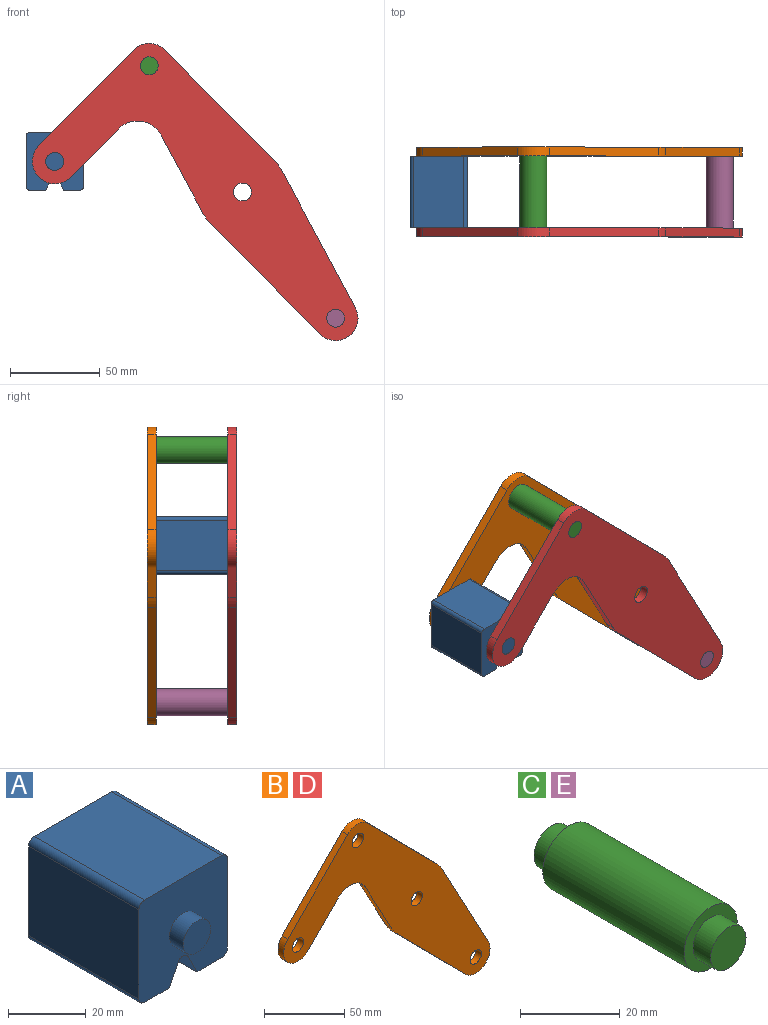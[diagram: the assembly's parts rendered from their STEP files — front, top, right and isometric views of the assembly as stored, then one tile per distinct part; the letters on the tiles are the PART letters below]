
ASSEMBLY  parts=5 mates=3
PART A: 18 faces, bbox 32.1x50x32.1 mm
  f0: plane 40x28.08mm, normal (1,0,0), area 1123.1mm2, adj f4,f10,f13,f14
  f1: plane 40x9.04mm, normal (0,0,-1), area 361.6mm2, adj f2,f4,f10,f14
  f2: plane 40x6.42mm, normal (-0.89,0,-0.45), area 287.2mm2, adj f1,f4,f10,f15
  f3: plane 40x6.42mm, normal (0.89,0,-0.45), area 287.2mm2, adj f4,f5,f10,f15
  f4: plane 32.08x32.08mm, normal (0,-1,0), area 900.6mm2, adj f0,f1,f2,f3,f5,f6,f7,f9
  f5: plane 40x9.04mm, normal (0,0,-1), area 361.6mm2, adj f3,f4,f10,f16
  f6: plane 40x28.08mm, normal (0,0,1), area 1123.1mm2, adj f4,f10,f13,f17
  f7: plane 40x28.08mm, normal (-1,0,0), area 1123.1mm2, adj f4,f10,f16,f17
  f8: plane 10x10mm, normal (0,-1,0), area 78.5mm2, adj f9
  f9: cylinder r=5mm len=10mm, axis (0,1,0), area 157.1mm2, adj f4,f8
  f10: plane 32.08x32.08mm, normal (0,1,0), area 900.6mm2, adj f0,f1,f2,f3,f5,f6,f7,f12
  f11: plane 10x10mm, normal (0,1,0), area 78.5mm2, adj f12
  f12: cylinder r=5mm len=10mm, axis (0,-1,0), area 157.1mm2, adj f10,f11
  f13: cylinder r=2mm len=40mm, axis (0,1,0), area 125.7mm2, adj f0,f4,f6,f10
  f14: cylinder r=2mm len=40mm, axis (0,-1,0), area 125.7mm2, adj f0,f1,f4,f10
  f15: cylinder r=2mm len=40mm, axis (0,1,0), area 177.1mm2, adj f2,f3,f4,f10
  f16: cylinder r=2mm len=40mm, axis (0,1,0), area 125.7mm2, adj f4,f5,f7,f10
  f17: cylinder r=2mm len=40mm, axis (0,-1,0), area 125.7mm2, adj f4,f6,f7,f10
PART B: 18 faces, bbox 181.7x5x165.8 mm
  f0: plane 43.49x23.35mm, normal (-0.88,0,-0.47), area 246.8mm2, adj f1,f14,f16,f17
  f1: cylinder r=25mm len=5.75mm, axis (0,1,0), area 35.8mm2, adj f0,f2,f16,f17
  f2: plane 61.6x60.87mm, normal (-0.71,0,-0.7), area 433mm2, adj f1,f3,f16,f17
  f3: cylinder r=12.5mm len=21.39mm, axis (0,1,0), area 178.4mm2, adj f2,f4,f16,f17
  f4: plane 76.3x40.96mm, normal (0.88,0,0.47), area 433mm2, adj f3,f5,f16,f17
  f5: cylinder r=25mm len=5.75mm, axis (0,1,0), area 35.8mm2, adj f4,f6,f16,f17
  f6: plane 61.6x60.87mm, normal (0.71,0,0.7), area 433mm2, adj f5,f7,f16,f17
  f7: cylinder r=12.5mm len=17.78mm, axis (0,1,0), area 98.9mm2, adj f6,f8,f16,f17
  f8: plane 53.35x52.71mm, normal (-0.71,0,0.7), area 375mm2, adj f7,f9,f16,f17
  f9: cylinder r=12.5mm len=21.39mm, axis (0,1,0), area 196.3mm2, adj f8,f10,f16,f17
  f10: plane 26.86x26.54mm, normal (0.71,0,-0.7), area 188.8mm2, adj f9,f14,f16,f17
  f11: cylinder r=5mm len=10mm, axis (0,1,0), area 157.1mm2, adj f16,f17
  f12: cylinder r=5mm len=10mm, axis (0,1,0), area 157.1mm2, adj f16,f17
  f13: cylinder r=5mm len=10mm, axis (0,1,0), area 157.1mm2, adj f16,f17
  f14: cylinder r=15mm len=23.89mm, axis (0,1,0), area 140.2mm2, adj f0,f10,f16,f17
  f15: cylinder r=5mm len=10mm, axis (0,1,0), area 157.1mm2, adj f16,f17
  f16: plane 181.66x165.78mm, normal (0,-1,0), area 8710.1mm2, adj f0,f1,f2,f3,f4,f5,f6,f7
  f17: plane 181.66x165.78mm, normal (0,1,0), area 8710.1mm2, adj f0,f1,f2,f3,f4,f5,f6,f7
PART C: 7 faces, bbox 15x50x15 mm
  f0: cylinder r=7.5mm len=40mm, axis (0,-1,0), area 1885mm2, adj f2,f5
  f1: cylinder r=5mm len=10mm, axis (0,1,0), area 157.1mm2, adj f2,f3
  f2: plane 15x15mm, normal (0,-1,0), area 98.2mm2, adj f0,f1
  f3: plane 10x10mm, normal (0,-1,0), area 78.5mm2, adj f1
  f4: cylinder r=5mm len=10mm, axis (0,-1,0), area 157.1mm2, adj f5,f6
  f5: plane 15x15mm, normal (0,1,0), area 98.2mm2, adj f0,f4
  f6: plane 10x10mm, normal (0,1,0), area 78.5mm2, adj f4
PART D: same geometry as B
PART E: same geometry as C
PLACE A t=(0,-20,0)mm
PLACE B t=(0,25,0)mm
PLACE C t=(0,-20,0)mm
PLACE D t=(0,-20,0)mm fixed
PLACE E t=(103.95,-20,-140.78)mm
MATE revolute A.f9 <-> D.f9  axis (0,1,0) through (-104.69,-20,17.04)mm
MATE fastened E.f0 <-> D.f3  axis (0,-1,0) through (51.98,-20,-70.39)mm
MATE fastened C.f0 <-> B.f7  axis (0,-1,0) through (-51.98,20,70.39)mm
